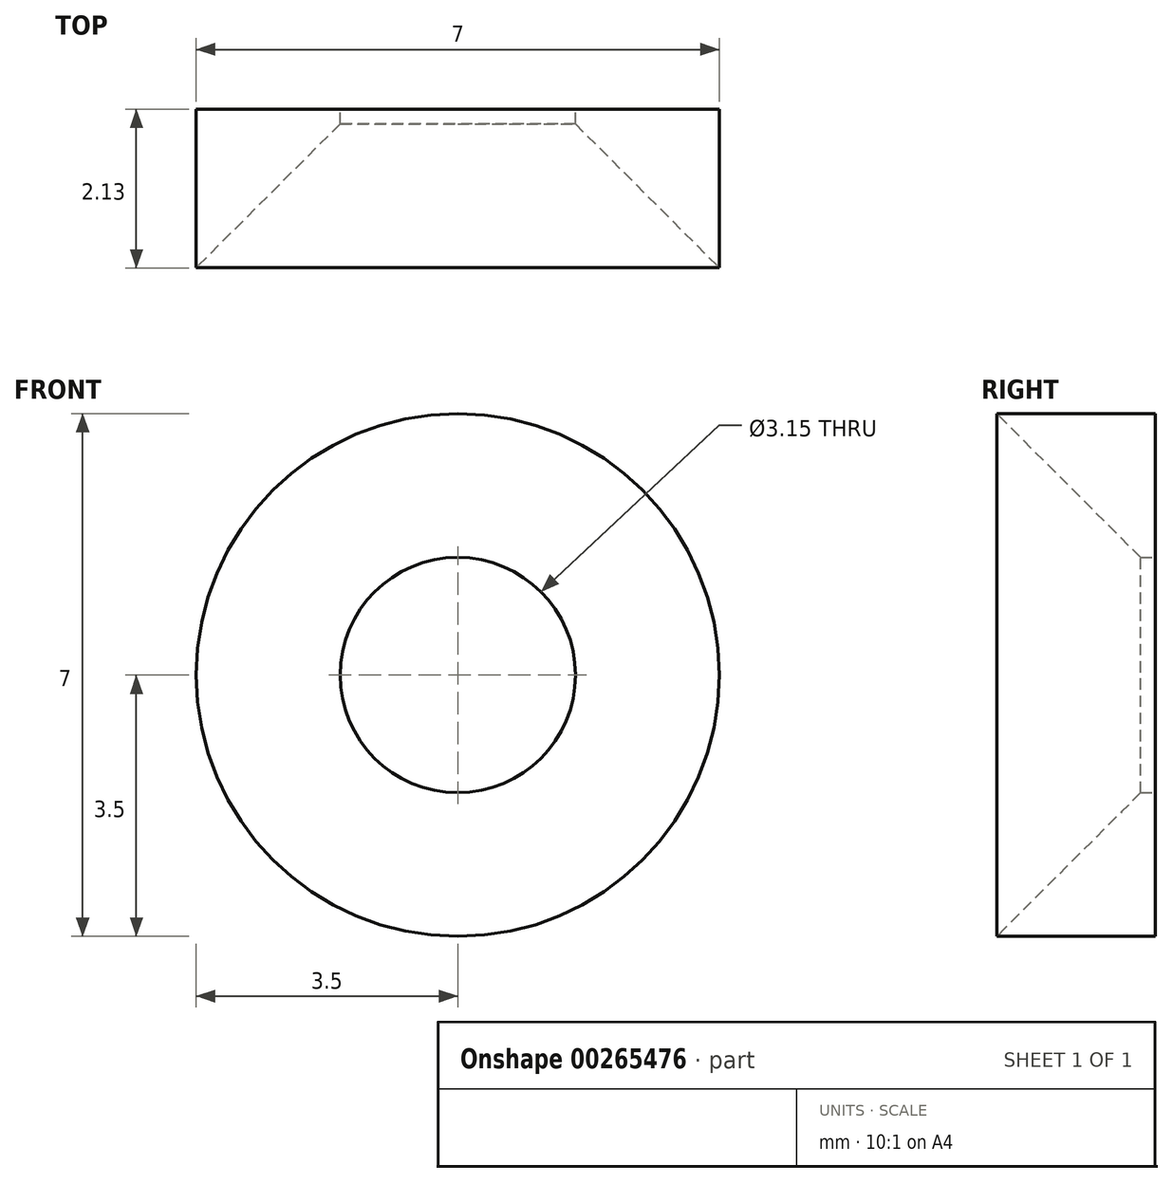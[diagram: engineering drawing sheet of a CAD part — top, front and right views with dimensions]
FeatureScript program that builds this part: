
annotation { "Feature Type Name" : "Feature", "Feature Type Description" : "" }
export const myFeature = defineFeature(function(context is Context, id is Id, definition is map)
    precondition{}
    {
        {
            var Q0;
            Q0=qCreatedBy(makeId("Front.planeOp"),FACE);
            var sketch = newSketch(context, id + "F0", { "sketchPlane" : qUnion([Q0])});
            skCircle(sketch, "E0", {"center": v(0, 0) * mm, "radius": 3.5 * mm});
            skCircle(sketch, "E1", {"center": v(0, 0) * mm, "radius": 1.57 * mm});
            skSolve(sketch);
        }
        {
            var Q0;
            Q0=makeQuery(id+"F0.imprint","IMPRINT",FACE,{"disambiguationData":[TD([[makeQuery(id+"F0.imprint","IMPRINT",EDGE,{"derivedFrom":sQuery(id+"F0.wireOp",EDGE,"E0")}),1.0]])]});
            var Q1;
            Q1=makeQuery(id+"F0.imprint","IMPRINT",FACE,{"disambiguationData":[TD([[makeQuery(id+"F0.imprint","IMPRINT",EDGE,{"derivedFrom":sQuery(id+"F0.wireOp",EDGE,"E1")}),1.0]])]});
            extrude(context, id + "F1", {"entities" : qUnion([Q0, Q1]), "depth" : 2.2 * mm});
        }
        {
            var Q0;
            Q0=makeQuery(id+"F0.imprint","IMPRINT",FACE,{"disambiguationData":[TD([[makeQuery(id+"F0.imprint","IMPRINT",EDGE,{"derivedFrom":sQuery(id+"F0.wireOp",EDGE,"E1")}),1.0]])]});
            var Q1;
            Q1=sQuery(id+"F0.wireOp",EDGE,"E1");
            extrude(context, id + "F2", {"entities" : qUnion([Q0]), "operationType" : NewBodyOperationType.REMOVE, "surfaceEntities" : qUnion([Q1]), "depth" : 4 * mm});
        }
        {
            var Q0;
            Q0=makeQuery(id+"F2.boolean.opBoolean","INTERSECT",EDGE,{"derivedFrom":[makeQuery(id+"F1.opExtrude","CAP_FACE",FACE,{"disambiguationData":[OSD([sQuery(id+"F0.wireOp",EDGE,"E0")])],"isStart":false}),makeQuery(id+"F2.opExtrude","SWEPT_FACE",FACE,{"disambiguationData":[OSD([sQuery(id+"F0.wireOp",EDGE,"E1")])]})]});
            chamfer(context, id + "F3", {"entities" : qUnion([Q0]), "width" : 2 * mm});
        }
    });
